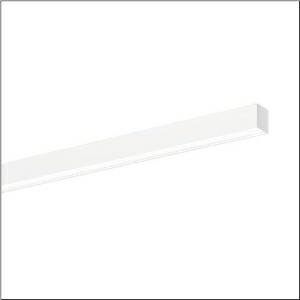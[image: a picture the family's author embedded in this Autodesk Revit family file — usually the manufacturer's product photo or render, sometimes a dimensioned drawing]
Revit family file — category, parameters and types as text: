
# Revit family: silica_r__21_51mx23dc3awb_8ef9
name_source: partatom
category: Lighting Fixtures
units: mm (PartAtom-declared; Revit-internal decimal feet)

## family parameters
Cut with Voids When Loaded = No
Host = Face
Light Source = No
Part Type = Normal
Room Calculation Point = No
Round Connector Dimension = Use Diameter
Shared = No

## types (1)
- --- (1 x LED, 8200 lm, 62.2 W, 3000K)
    Apparent Load = 62 VA
    CIE Flux Codes = 78 96 99 100 100
    Color Rendering = 80
    Color Temperature = 3000K
    Default Elevation = 1800 mm
    Description = Silica® 21, office luminaire, primary optical cover: prismatic diffuser, of PMMA, CAT 2 (L<= 3000cd/m²), light emission: direct distribution, primary light characteristic: symmetric, installation type: surface-mounted, LED, rated luminous flux: 8.200lm, luminous efficacy: 132lm/W, light colour: 830, colour temperature: 3000K, control gear: DALI 2, with terminal, 3+2-pole, max. 2.5mm², mains connection: 220..240V, AC, 50/60Hz, rated input power: 62.2W, luminaire housing, of aluminium, traffic white (RAL 9016), length: 3.004mm, width: 53mm, height: 53mm, protection rating (complete): IP20, insulation class (complete): insulation class I (protective earthing), certification: CE, permissible operating ambient temperature: 0..+35°C, standard: EN 50419, packaging unit: 1 piece
    Height = 53 mm
    Lamp = 1 x LED
    Lamp Light Flux = 8200 lm
    Lamp Power = 62.2 W
    Lamp count = 1
    Length = 3004 mm
    Luminous efficacy = 132 lm/W
    Manufacturer = Siteco
    ModVariant = No
    Model = 51MX23DC3AWB
    Mounting Place = Ceiling
    Mounting Type = Surface mounted
    Number of Poles = 1
    OnlyDefault = Yes
    Power Factor = 1
    Product Name = Silica® 21
    Product group = office luminaire | ceiling mounted
    ProductGroupID = 302
    Protection Class = Protection class I
    Protection Degree = IP 20
    RLX_Detail_Level = 1
    RLX_Emergency_Light_Flux = 0 lm
    RLX_Emergency_Type = 0
    RLX_Emergency_Type_DB = No
    RlxData = <blob elided: 18721 chars, md5=0baf5adc>
    Socket = socket
    Standby Power = 0 W
    System Light Flux = 8200 lm
    System Power = 62 W
    Type Comments = factory setting: luminous flux: 100 % | dim-lin: 254 | 345 mA
    Type Image = l_1335877.jpg
    URL = http://relux.com
    VarID = @adj_119464
    Voltage = 0 V
    Weight = 0.00 kg
    Width = 53 mm

## geometry (parser evidence)
native form markers: Blend x4, Sweep x10
no freeform markers — native parametric forms only
